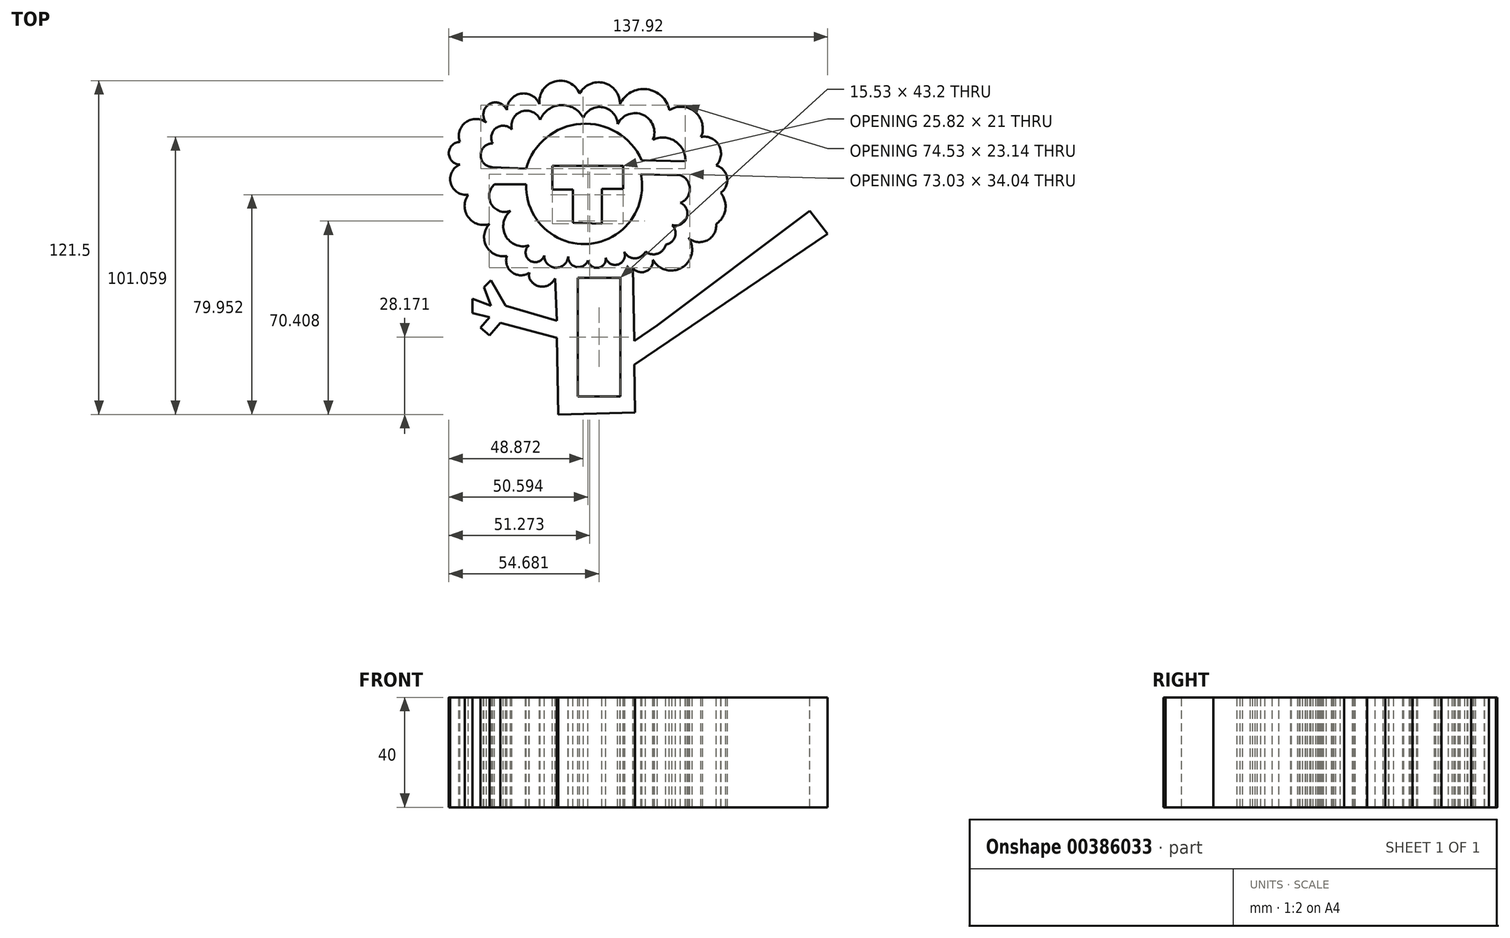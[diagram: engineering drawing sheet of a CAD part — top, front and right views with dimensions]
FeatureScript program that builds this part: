
annotation { "Feature Type Name" : "Feature", "Feature Type Description" : "" }
export const myFeature = defineFeature(function(context is Context, id is Id, definition is map)
    precondition{}
    {
        {
            var Q0;
            Q0=qCreatedBy(makeId("Top.planeOp"),FACE);
            var sketch = newSketch(context, id + "F0", { "sketchPlane" : qUnion([Q0])});
            skArc(sketch, "E0", {"start": v(-39.46, 41.9) * mm, "mid": v(-46.96, 42.1) * mm, "end": v(-49.07, 34.9) * mm});
            skArc(sketch, "E1", {"start": v(-32, 46.48) * mm, "mid": v(-38.46, 48.63) * mm, "end": v(-39.46, 41.9) * mm});
            skArc(sketch, "E2", {"start": v(-20.12, 48.63) * mm, "mid": v(-26.95, 52.47) * mm, "end": v(-32, 46.48) * mm});
            skPoint(sketch, "E2.startSnap0", {"position": v(-38.46, 48.63) * mm});
            skArc(sketch, "E3", {"start": v(-5.49, 52.47) * mm, "mid": v(-14.48, 56.95) * mm, "end": v(-20.12, 48.63) * mm});
            skPoint(sketch, "E3.startSnap0", {"position": v(-26.95, 52.47) * mm});
            skArc(sketch, "E4", {"start": v(9.14, 48.63) * mm, "mid": v(3.36, 56.38) * mm, "end": v(-5.49, 52.47) * mm});
            skArc(sketch, "E5", {"start": v(27.13, 46.48) * mm, "mid": v(18.92, 54.1) * mm, "end": v(9.14, 48.63) * mm});
            skArc(sketch, "E6", {"start": v(38.7, 36.73) * mm, "mid": v(36.5, 45.86) * mm, "end": v(27.13, 46.48) * mm});
            skArc(sketch, "E7", {"start": v(44.2, 26.37) * mm, "mid": v(45.27, 33.57) * mm, "end": v(38.7, 36.73) * mm});
            skArc(sketch, "E8", {"start": v(34.14, 0) * mm, "mid": v(40.9, -0.92) * mm, "end": v(44.2, 5.06) * mm});
            skArc(sketch, "E9", {"start": v(21.18, -8) * mm, "mid": v(31.84, -10.78) * mm, "end": v(34.14, 0) * mm});
            skArc(sketch, "E10", {"start": v(-46.02, 15.7) * mm, "mid": v(-46.07, 7.53) * mm, "end": v(-38.29, 5.06) * mm});
            skArc(sketch, "E11", {"start": v(-38.29, 5.06) * mm, "mid": v(-39.47, -3.09) * mm, "end": v(-32, -6.55) * mm});
            skArc(sketch, "E12", {"start": v(13.86, -10.96) * mm, "mid": v(18.63, -12.21) * mm, "end": v(21.18, -8) * mm});
            skLineSegment(sketch, "E13", {"start": v(14.63, -63.55) * mm, "end": v(14.4, -46.15) * mm});
            skLineSegment(sketch, "E14", {"start": v(14.4, -46.15) * mm, "end": v(26.83, -37.73) * mm});
            skLineSegment(sketch, "E15", {"start": v(22.82, -31.81) * mm, "end": v(14.4, -37.51) * mm});
            skLineSegment(sketch, "E16", {"start": v(14.4, -37.51) * mm, "end": v(13.86, -10.96) * mm});
            skLineSegment(sketch, "E17", {"start": v(84.78, 1.49) * mm, "end": v(78.34, 9.87) * mm});
            skLineSegment(sketch, "E18", {"start": v(22.82, -31.81) * mm, "end": v(78.34, 9.87) * mm});
            skLineSegment(sketch, "E19", {"start": v(-13.35, -64.3) * mm, "end": v(-13.79, -36.38) * mm});
            skArc(sketch, "E20", {"start": v(8.36, 41.5) * mm, "mid": v(2.96, 47.52) * mm, "end": v(-4.18, 43.73) * mm});
            skArc(sketch, "E21", {"start": v(21.19, 35.69) * mm, "mid": v(17.57, 44.76) * mm, "end": v(8.36, 41.5) * mm});
            skArc(sketch, "E22", {"start": v(33, 27.9) * mm, "mid": v(29.31, 35.15) * mm, "end": v(21.19, 35.69) * mm});
            skArc(sketch, "E23", {"start": v(31.19, 12.75) * mm, "mid": v(34.65, 17.77) * mm, "end": v(31.19, 22.78) * mm});
            skArc(sketch, "E24", {"start": v(28.12, 4.67) * mm, "mid": v(33.46, 7.27) * mm, "end": v(31.19, 12.75) * mm});
            skArc(sketch, "E25", {"start": v(-37.16, 34.4) * mm, "mid": v(-41.53, 30.07) * mm, "end": v(-37.16, 25.75) * mm});
            skArc(sketch, "E26", {"start": v(-23.77, -12.65) * mm, "mid": v(-23.92, -13.72) * mm, "end": v(-23.77, -14.78) * mm});
            skLineSegment(sketch, "E27", {"start": v(84.78, 1.49) * mm, "end": v(26.83, -37.73) * mm});
            skLineSegment(sketch, "E28", {"start": v(-13.35, -64.3) * mm, "end": v(14.63, -63.55) * mm});
            skArc(sketch, "E29", {"start": v(-32, -6.55) * mm, "mid": v(-30.1, -12.58) * mm, "end": v(-23.77, -12.65) * mm});
            skPoint(sketch, "E30", {"position": v(-12.63, -36.38) * mm});
            skPoint(sketch, "E31.endSnap0", {"position": v(-34.48, 7.12) * mm});
            skLineSegment(sketch, "E32.bottom", {"start": v(-6.23, -14.53) * mm, "end": v(9.3, -14.53) * mm});
            skLineSegment(sketch, "E32.top", {"start": v(-6.23, -57.73) * mm, "end": v(9.3, -57.73) * mm});
            skLineSegment(sketch, "E32.left", {"start": v(-6.23, -14.53) * mm, "end": v(-6.23, -57.73) * mm});
            skLineSegment(sketch, "E32.right", {"start": v(9.3, -14.53) * mm, "end": v(9.3, -57.73) * mm});
            skArc(sketch, "E33", {"start": v(25.87, -2.44) * mm, "mid": v(29.2, 0.41) * mm, "end": v(28.12, 4.67) * mm});
            skArc(sketch, "E34", {"start": v(18.46, -5.02) * mm, "mid": v(22.87, -5.76) * mm, "end": v(25.87, -2.44) * mm});
            skLineSegment(sketch, "E35", {"start": v(-13.74, -30.2) * mm, "end": v(-32.4, -24.73) * mm});
            skLineSegment(sketch, "E36", {"start": v(-32.4, -24.73) * mm, "end": v(-37.75, -15.45) * mm});
            skLineSegment(sketch, "E37", {"start": v(-37.75, -15.45) * mm, "end": v(-40.3, -18) * mm});
            skLineSegment(sketch, "E38", {"start": v(-40.3, -18) * mm, "end": v(-37.75, -24.73) * mm});
            skLineSegment(sketch, "E39", {"start": v(-37.75, -24.73) * mm, "end": v(-44.56, -22.25) * mm});
            skLineSegment(sketch, "E40", {"start": v(-44.56, -22.25) * mm, "end": v(-44.56, -27.36) * mm});
            skLineSegment(sketch, "E41", {"start": v(-44.56, -27.36) * mm, "end": v(-38.3, -28.88) * mm});
            skLineSegment(sketch, "E42", {"start": v(-38.3, -28.88) * mm, "end": v(-41.56, -32.7) * mm});
            skLineSegment(sketch, "E43", {"start": v(-41.56, -32.7) * mm, "end": v(-38.3, -35.49) * mm});
            skLineSegment(sketch, "E44", {"start": v(-38.3, -35.49) * mm, "end": v(-34.44, -30.96) * mm});
            skLineSegment(sketch, "E45", {"start": v(-34.44, -30.96) * mm, "end": v(-13.79, -36.38) * mm});
            skLineSegment(sketch, "E46", {"start": v(-36.51, 19.45) * mm, "end": v(-25, 19.45) * mm});
            skLineSegment(sketch, "E47", {"start": v(-37.16, 25.75) * mm, "end": v(-25, 25.2) * mm});
            skLineSegment(sketch, "E48", {"start": v(16.77, 23.13) * mm, "end": v(31.19, 22.78) * mm});
            skLineSegment(sketch, "E49", {"start": v(33, 27.9) * mm, "end": v(17.03, 28.28) * mm});
            skArc(sketch, "E50", {"start": v(17.03, 28.28) * mm, "mid": v(-5.07, 41.5) * mm, "end": v(-25, 25.2) * mm});
            skArc(sketch, "E51", {"start": v(-25, 19.45) * mm, "mid": v(-2.04, -2.19) * mm, "end": v(16.77, 23.13) * mm});
            skLineSegment(sketch, "E52", {"start": v(10.37, 26.15) * mm, "end": v(-15.46, 26.15) * mm});
            skLineSegment(sketch, "E53", {"start": v(-15.46, 26.15) * mm, "end": v(-15.46, 17.62) * mm});
            skLineSegment(sketch, "E54", {"start": v(10.37, 26.15) * mm, "end": v(10.37, 17.78) * mm});
            skLineSegment(sketch, "E55", {"start": v(-15.46, 17.62) * mm, "end": v(-7.97, 17.62) * mm});
            skLineSegment(sketch, "E56", {"start": v(-7.97, 17.62) * mm, "end": v(-7.97, 5.47) * mm});
            skLineSegment(sketch, "E57", {"start": v(10.37, 17.78) * mm, "end": v(2.6, 17.78) * mm});
            skLineSegment(sketch, "E58", {"start": v(2.6, 17.78) * mm, "end": v(2.6, 5.15) * mm});
            skLineSegment(sketch, "E59", {"start": v(-7.97, 5.47) * mm, "end": v(2.6, 5.15) * mm});
            skArc(sketch, "E60", {"start": v(-29.1, 37.39) * mm, "mid": v(-34.86, 40.53) * mm, "end": v(-37.16, 34.4) * mm});
            skArc(sketch, "E61", {"start": v(-19.87, 42.98) * mm, "mid": v(-27.7, 45.5) * mm, "end": v(-29.1, 37.39) * mm});
            skArc(sketch, "E62", {"start": v(-4.18, 43.73) * mm, "mid": v(-12.27, 48.33) * mm, "end": v(-19.87, 42.98) * mm});
            skArc(sketch, "E63", {"start": v(-9.66, -6.8) * mm, "mid": v(-6.68, -10.6) * mm, "end": v(-2.46, -8.23) * mm});
            skArc(sketch, "E64", {"start": v(-2.46, -8.23) * mm, "mid": v(1.49, -10.87) * mm, "end": v(3.9, -6.8) * mm});
            skArc(sketch, "E65", {"start": v(3.9, -6.8) * mm, "mid": v(8.3, -9.75) * mm, "end": v(10.7, -5.02) * mm});
            skArc(sketch, "E66", {"start": v(-23.77, -14.78) * mm, "mid": v(-19.12, -17.77) * mm, "end": v(-14.47, -14.78) * mm});
            skLineSegment(sketch, "E67", {"start": v(-13.74, -30.2) * mm, "end": v(-14.47, -14.78) * mm});
            skArc(sketch, "E68", {"start": v(-36.51, 19.45) * mm, "mid": v(-37.63, 12.2) * mm, "end": v(-30.7, 9.8) * mm});
            skArc(sketch, "E69", {"start": v(-30.7, 9.8) * mm, "mid": v(-32.48, 0.76) * mm, "end": v(-23.98, -2.78) * mm});
            skArc(sketch, "E70", {"start": v(-23.98, -2.78) * mm, "mid": v(-23.1, -8.56) * mm, "end": v(-18.26, -5.3) * mm});
            skArc(sketch, "E71", {"start": v(-18.26, -5.3) * mm, "mid": v(-14.78, -10.8) * mm, "end": v(-9.66, -6.8) * mm});
            skArc(sketch, "E72", {"start": v(10.7, -5.02) * mm, "mid": v(14.58, -7.45) * mm, "end": v(18.46, -5.02) * mm});
            skArc(sketch, "E73", {"start": v(45.84, 16.4) * mm, "mid": v(48.2, 21.9) * mm, "end": v(44.2, 26.37) * mm});
            skArc(sketch, "E74", {"start": v(44.2, 5.06) * mm, "mid": v(47.55, 10.36) * mm, "end": v(45.84, 16.4) * mm});
            skArc(sketch, "E75", {"start": v(-49.07, 34.9) * mm, "mid": v(-53.14, 30.79) * mm, "end": v(-49.07, 26.67) * mm});
            skArc(sketch, "E76", {"start": v(-49.07, 26.67) * mm, "mid": v(-52.42, 19.83) * mm, "end": v(-46.02, 15.7) * mm});
            skSolve(sketch);
        }
        {
            var Q0;
            Q0=makeQuery(id+"F0.imprint","IMPRINT",FACE,{"disambiguationData":[TD([[makeQuery(id+"F0.imprint","IMPRINT",EDGE,{"derivedFrom":sQuery(id+"F0.wireOp",EDGE,"E0")}),1.0]])]});
            extrude(context, id + "F1", {"entities" : qUnion([Q0]), "oppositeDirection" : true, "depth" : 40 * mm});
        }
    });
